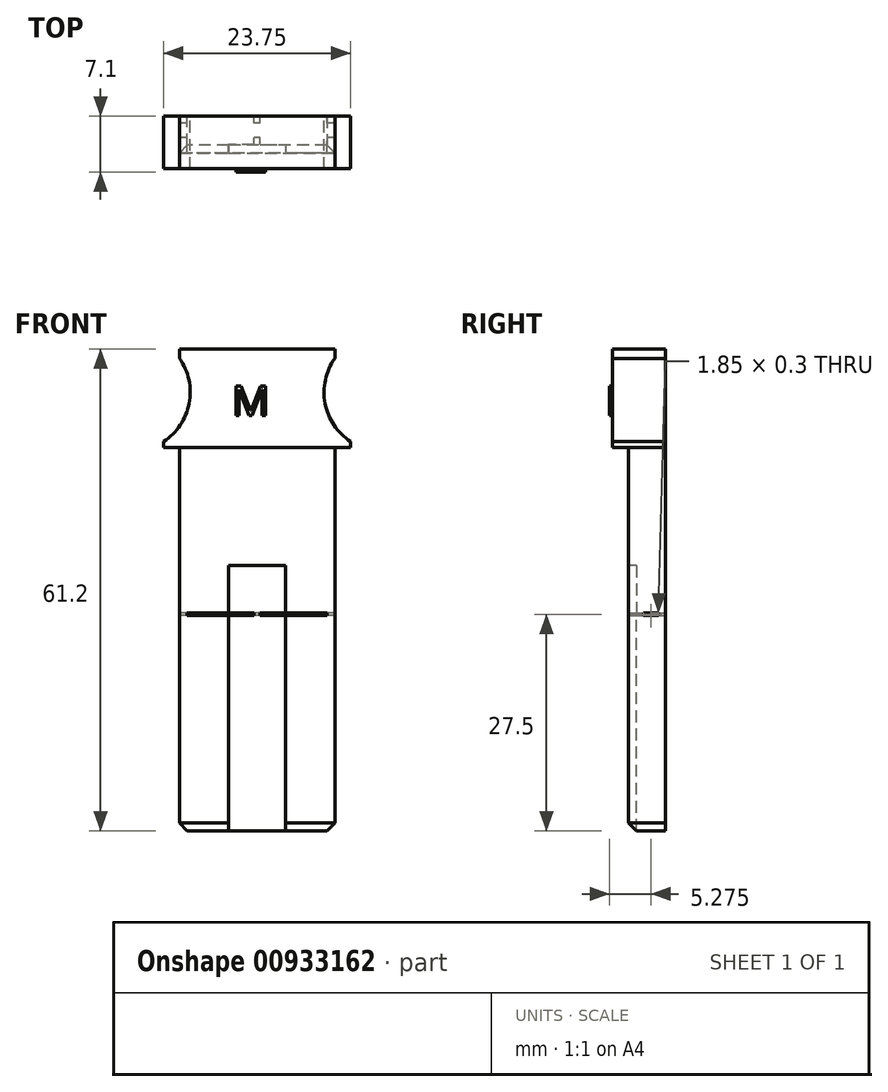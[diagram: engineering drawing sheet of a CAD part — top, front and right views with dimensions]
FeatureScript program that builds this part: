
annotation { "Feature Type Name" : "Feature", "Feature Type Description" : "" }
export const myFeature = defineFeature(function(context is Context, id is Id, definition is map)
    precondition{}
    {
        {
            var Q0;
            Q0=qCreatedBy(makeId("Front.planeOp"),FACE);
            var sketch = newSketch(context, id + "F0", { "sketchPlane" : qUnion([Q0])});
            skLineSegment(sketch, "E0.bottom", {"start": v(0, 0) * mm, "end": v(19.75, 0) * mm});
            skLineSegment(sketch, "E0.top", {"start": v(0, 61.2) * mm, "end": v(19.75, 61.2) * mm});
            skLineSegment(sketch, "E0.left", {"start": v(0, 0) * mm, "end": v(0, 61.2) * mm});
            skLineSegment(sketch, "E0.right", {"start": v(19.75, 0) * mm, "end": v(19.75, 61.2) * mm});
            skLineSegment(sketch, "E1", {"start": v(9.88, 61.2) * mm, "end": v(9.87, 0) * mm, "construction": true});
            skPoint(sketch, "E2", {"position": v(9.88, 34.7) * mm});
            skLineSegment(sketch, "E3", {"start": v(-7.67, 27.5) * mm, "end": v(34.9, 27.5) * mm, "construction": true});
            skLineSegment(sketch, "E4", {"start": v(0, 27.35) * mm, "end": v(0, 27.65) * mm});
            skCircle(sketch, "E5", {"center": v(25.88, 55.7) * mm, "radius": 7.5 * mm});
            skCircle(sketch, "E6.MirrorC", {"center": v(-6.13, 55.7) * mm, "radius": 7.5 * mm});
            skLineSegment(sketch, "E7.bottom", {"start": v(0, 27.65) * mm, "end": v(9.47, 27.65) * mm});
            skLineSegment(sketch, "E7.top", {"start": v(0, 27.65) * mm, "end": v(9.47, 27.65) * mm});
            skLineSegment(sketch, "E7.left", {"start": v(0, 27.65) * mm, "end": v(0, 27.65) * mm});
            skLineSegment(sketch, "E7.right", {"start": v(9.47, 27.65) * mm, "end": v(9.47, 27.65) * mm});
            skLineSegment(sketch, "E8", {"start": v(9.47, 27.65) * mm, "end": v(9.47, 27.35) * mm});
            skLineSegment(sketch, "E9", {"start": v(9.47, 27.35) * mm, "end": v(0, 27.35) * mm});
            skLineSegment(sketch, "E10", {"start": v(0, 27.65) * mm, "end": v(0, 27.35) * mm});
            skLineSegment(sketch, "E11.MirrorCS", {"start": v(19.75, 27.65) * mm, "end": v(10.28, 27.65) * mm});
            skLineSegment(sketch, "E12.MirrorCS", {"start": v(10.27, 27.65) * mm, "end": v(10.27, 27.35) * mm});
            skLineSegment(sketch, "E13.MirrorCS", {"start": v(10.28, 27.35) * mm, "end": v(19.75, 27.35) * mm});
            skLineSegment(sketch, "E14.MirrorCS", {"start": v(19.75, 27.65) * mm, "end": v(19.75, 27.35) * mm});
            skLineSegment(sketch, "E15.bottom", {"start": v(0, 48.7) * mm, "end": v(-2, 48.7) * mm});
            skLineSegment(sketch, "E15.top", {"start": v(0, 65.03) * mm, "end": v(-2, 65.03) * mm});
            skLineSegment(sketch, "E15.left", {"start": v(0, 48.7) * mm, "end": v(0, 65.03) * mm});
            skLineSegment(sketch, "E15.right", {"start": v(-2, 48.7) * mm, "end": v(-2, 65.03) * mm});
            skLineSegment(sketch, "E16.MirrorCS", {"start": v(19.75, 65.03) * mm, "end": v(21.75, 65.03) * mm});
            skLineSegment(sketch, "E17.MirrorCS", {"start": v(21.75, 48.7) * mm, "end": v(21.75, 65.03) * mm});
            skLineSegment(sketch, "E18.MirrorCS", {"start": v(19.75, 48.7) * mm, "end": v(21.75, 48.7) * mm});
            skLineSegment(sketch, "E19", {"start": v(1, 27.65) * mm, "end": v(1, 27.35) * mm});
            skLineSegment(sketch, "E20.MirrorCS", {"start": v(18.75, 27.65) * mm, "end": v(18.75, 27.35) * mm});
            skSolve(sketch);
        }
        {
            var Q0;
            {var subQ4=sQuery(id+"F0.wireOp",EDGE,"E0.bottom");Q0=makeQuery(id+"F0.imprint","IMPRINT",FACE,{"disambiguationData":[TD([[makeQuery(id+"F0.imprint","IMPRINT",EDGE,{"derivedFrom":subQ4}),1.0]])]});}
            var Q1;
            {var subQ0=sQuery(id+"F0.wireOp",EDGE,"E15.bottom");Q1=makeQuery(id+"F0.imprint","IMPRINT",FACE,{"disambiguationData":[TD([[makeQuery(id+"F0.imprint","IMPRINT",EDGE,{"derivedFrom":subQ0}),-1.0]])]});}
            var Q2;
            {var subQ0=sQuery(id+"F0.wireOp",EDGE,"E18.MirrorCS");Q2=makeQuery(id+"F0.imprint","IMPRINT",FACE,{"disambiguationData":[TD([[makeQuery(id+"F0.imprint","IMPRINT",EDGE,{"derivedFrom":subQ0}),1.0]])]});}
            var Q3;
            {var subQ5=sQuery(id+"F0.wireOp",EDGE,"E19");Q3=makeQuery(id+"F0.imprint","IMPRINT",FACE,{"disambiguationData":[TD([[makeQuery(id+"F0.imprint","IMPRINT",EDGE,{"derivedFrom":subQ5}),-1.0]])]});}
            var Q4;
            {var subQ5=sQuery(id+"F0.wireOp",EDGE,"E20.MirrorCS");Q4=makeQuery(id+"F0.imprint","IMPRINT",FACE,{"disambiguationData":[TD([[makeQuery(id+"F0.imprint","IMPRINT",EDGE,{"derivedFrom":subQ5}),1.0]])]});}
            extrude(context, id + "F1", {"entities" : qUnion([Q0, Q1, Q2, Q3, Q4]), "depth" : 4.7 * mm, "offsetDistance" : 25 * mm});
        }
        {
            var Q0;
            Q0=makeQuery(id+"F1.opExtrude","CAP_FACE",FACE,{"disambiguationData":[OSD([sQuery(id+"F0.wireOp",EDGE,"E0.bottom"),sQuery(id+"F0.wireOp",EDGE,"E0.top"),sQuery(id+"F0.wireOp",EDGE,"E0.left"),sQuery(id+"F0.wireOp",EDGE,"E0.right"),sQuery(id+"F0.wireOp",EDGE,"E5"),sQuery(id+"F0.wireOp",EDGE,"E6.MirrorC"),sQuery(id+"F0.wireOp",EDGE,"E7.bottom"),sQuery(id+"F0.wireOp",EDGE,"E8"),sQuery(id+"F0.wireOp",EDGE,"E9"),sQuery(id+"F0.wireOp",EDGE,"E11.MirrorCS"),sQuery(id+"F0.wireOp",EDGE,"E12.MirrorCS"),sQuery(id+"F0.wireOp",EDGE,"E13.MirrorCS"),sQuery(id+"F0.wireOp",EDGE,"E15.bottom"),sQuery(id+"F0.wireOp",EDGE,"E15.right"),sQuery(id+"F0.wireOp",EDGE,"E17.MirrorCS"),sQuery(id+"F0.wireOp",EDGE,"E18.MirrorCS"),sQuery(id+"F0.wireOp",EDGE,"E19"),sQuery(id+"F0.wireOp",EDGE,"E20.MirrorCS")])],"isStart":false});
            var sketch = newSketch(context, id + "F2", { "sketchPlane" : qUnion([Q0])});
            skLineSegment(sketch, "E21", {"start": v(6.28, 33.7) * mm, "end": v(13.48, 33.7) * mm});
            skLineSegment(sketch, "E22", {"start": v(13.48, 33.7) * mm, "end": v(13.48, 2.2) * mm});
            skLineSegment(sketch, "E23", {"start": v(13.48, 2.2) * mm, "end": v(13.48, 2.2) * mm});
            skLineSegment(sketch, "E24", {"start": v(13.48, 2.2) * mm, "end": v(13.48, 0) * mm});
            skLineSegment(sketch, "E25", {"start": v(13.48, 0) * mm, "end": v(6.28, 0) * mm});
            skLineSegment(sketch, "E26", {"start": v(6.28, 0) * mm, "end": v(6.28, 2.2) * mm});
            skLineSegment(sketch, "E27", {"start": v(6.28, 2.2) * mm, "end": v(6.28, 2.2) * mm});
            skLineSegment(sketch, "E28", {"start": v(6.28, 2.2) * mm, "end": v(6.28, 33.7) * mm});
            skLineSegment(sketch, "E29", {"start": v(9.88, 61.2) * mm, "end": v(9.88, 0) * mm, "construction": true});
            skSolve(sketch);
        }
        {
            var Q0;
            Q0=qSketchRegion(id+"F2",true);
            extrude(context, id + "F3", {"entities" : qUnion([Q0]), "operationType" : NewBodyOperationType.REMOVE, "oppositeDirection" : true, "depth" : 1.05 * mm, "offsetDistance" : 25 * mm});
        }
        {
            var Q0;
            {var subQ0=sQuery(id+"F0.wireOp",EDGE,"E0.right");Q0=makeQuery(id+"F1.opExtrude","SWEPT_FACE",FACE,{"disambiguationData":[OSD([subQ0]),TDD([makeQuery(id+"F0.imprint","IMPRINT",EDGE,{"disambiguationData":[TD([[makeQuery(id+"F0.imprint","INTERSECT",VERTEX,{"derivedFrom":[sQuery(id+"F0.wireOp",EDGE,"E0.top"),subQ0]}),1.0]])],"derivedFrom":subQ0})])]});}
            var sketch = newSketch(context, id + "F4", { "sketchPlane" : qUnion([Q0])});
            skLineSegment(sketch, "E30", {"start": v(-15.64, 31.3) * mm, "end": v(17.74, 31.3) * mm, "construction": true});
            skLineSegment(sketch, "E31", {"start": v(-1, 31.3) * mm, "end": v(0, 32.3) * mm});
            skLineSegment(sketch, "E32", {"start": v(0, 32.3) * mm, "end": v(0, 30.3) * mm});
            skLineSegment(sketch, "E33", {"start": v(0, 30.3) * mm, "end": v(-1, 31.3) * mm});
            skSolve(sketch);
        }
        {
            var Q0;
            Q0=makeQuery(id+"F1.opExtrude","CAP_FACE",FACE,{"disambiguationData":[OSD([sQuery(id+"F0.wireOp",EDGE,"E0.bottom"),sQuery(id+"F0.wireOp",EDGE,"E0.top"),sQuery(id+"F0.wireOp",EDGE,"E0.left"),sQuery(id+"F0.wireOp",EDGE,"E0.right"),sQuery(id+"F0.wireOp",EDGE,"E5"),sQuery(id+"F0.wireOp",EDGE,"E6.MirrorC"),sQuery(id+"F0.wireOp",EDGE,"E7.bottom"),sQuery(id+"F0.wireOp",EDGE,"E8"),sQuery(id+"F0.wireOp",EDGE,"E9"),sQuery(id+"F0.wireOp",EDGE,"E11.MirrorCS"),sQuery(id+"F0.wireOp",EDGE,"E12.MirrorCS"),sQuery(id+"F0.wireOp",EDGE,"E13.MirrorCS"),sQuery(id+"F0.wireOp",EDGE,"E15.bottom"),sQuery(id+"F0.wireOp",EDGE,"E15.right"),sQuery(id+"F0.wireOp",EDGE,"E17.MirrorCS"),sQuery(id+"F0.wireOp",EDGE,"E18.MirrorCS"),sQuery(id+"F0.wireOp",EDGE,"E19"),sQuery(id+"F0.wireOp",EDGE,"E20.MirrorCS")])],"isStart":false});
            var sketch = newSketch(context, id + "F5", { "sketchPlane" : qUnion([Q0])});
            skLineSegment(sketch, "E34", {"start": v(0, 48.7) * mm, "end": v(19.75, 48.7) * mm});
            skSolve(sketch);
        }
        {
            var Q0;
            Q0=makeQuery(id+"F5.imprint","IMPRINT",FACE,{"disambiguationData":[TD([[makeQuery(id+"F5.imprint","IMPRINT",EDGE,{"derivedFrom":sQuery(id+"F5.wireOp",EDGE,"E34")}),1.0]])]});
            extrude(context, id + "F6", {"entities" : qUnion([Q0]), "operationType" : NewBodyOperationType.ADD, "depth" : 2 * mm, "offsetDistance" : 25 * mm});
        }
        {
            var Q0;
            Q0=makeQuery(id+"F1.opExtrude","SWEPT_EDGE",EDGE,{"disambiguationData":[OSD([sQuery(id+"F0.wireOp",EDGE,"E0.bottom"),sQuery(id+"F0.wireOp",EDGE,"E0.left")])]});
            var Q1;
            Q1=makeQuery(id+"F1.opExtrude","SWEPT_EDGE",EDGE,{"disambiguationData":[OSD([sQuery(id+"F0.wireOp",EDGE,"E0.bottom"),sQuery(id+"F0.wireOp",EDGE,"E0.right")])]});
            var Q2;
            {var subQ0=sQuery(id+"F0.wireOp",EDGE,"E0.bottom");Q2=makeQuery(id+"F3.boolean.opBoolean","SPLIT",EDGE,{"disambiguationData":[TD([makeQuery(id+"F3.opExtrude","SWEPT_FACE",FACE,{"disambiguationData":[OSD([sQuery(id+"F2.wireOp",EDGE,"E26"),sQuery(id+"F2.wireOp",EDGE,"E28")])]})])],"derivedFrom":makeQuery(id+"F1.opExtrude","CAP_EDGE",EDGE,{"disambiguationData":[OSD([subQ0])],"isStart":false})});}
            var Q3;
            {var subQ0=sQuery(id+"F0.wireOp",EDGE,"E0.bottom");Q3=makeQuery(id+"F3.boolean.opBoolean","SPLIT",EDGE,{"disambiguationData":[TD([makeQuery(id+"F3.opExtrude","SWEPT_FACE",FACE,{"disambiguationData":[OSD([sQuery(id+"F2.wireOp",EDGE,"E22"),sQuery(id+"F2.wireOp",EDGE,"E24")])]})])],"derivedFrom":makeQuery(id+"F1.opExtrude","CAP_EDGE",EDGE,{"disambiguationData":[OSD([subQ0])],"isStart":false})});}
            var Q4;
            Q4=makeQuery(id+"F3.boolean.opBoolean","COPY",EDGE,{"derivedFrom":makeQuery(id+"F3.opExtrude","CAP_EDGE",EDGE,{"disambiguationData":[OSD([sQuery(id+"F2.wireOp",EDGE,"E25")])],"isStart":false})});
            chamfer(context, id + "F7", {"entities" : qUnion([Q0, Q1, Q2, Q3, Q4]), "width" : 1 * mm, "tangentPropagation" : true});
        }
        {
            var Q0;
            Q0=makeQuery(id+"F1.opExtrude","SWEPT_FACE",FACE,{"disambiguationData":[OSD([sQuery(id+"F0.wireOp",EDGE,"E8")])]});
            var sketch = newSketch(context, id + "F8", { "sketchPlane" : qUnion([Q0])});
            skLineSegment(sketch, "E35.bottom", {"start": v(0.9, 27.65) * mm, "end": v(2.75, 27.65) * mm});
            skLineSegment(sketch, "E35.top", {"start": v(0.9, 27.35) * mm, "end": v(2.75, 27.35) * mm});
            skLineSegment(sketch, "E35.left", {"start": v(0.9, 27.65) * mm, "end": v(0.9, 27.35) * mm});
            skLineSegment(sketch, "E35.right", {"start": v(2.75, 27.65) * mm, "end": v(2.75, 27.35) * mm});
            skLineSegment(sketch, "E36", {"start": v(0, 27.65) * mm, "end": v(0.9, 27.65) * mm, "construction": true});
            skLineSegment(sketch, "E37", {"start": v(2.75, 27.65) * mm, "end": v(3.65, 27.65) * mm, "construction": true});
            skSolve(sketch);
        }
        {
            var Q0;
            Q0=qSketchRegion(id+"F8",true);
            extrude(context, id + "F9", {"entities" : qUnion([Q0]), "operationType" : NewBodyOperationType.REMOVE, "endBound" : BoundingType.SYMMETRIC, "oppositeDirection" : true, "depth" : 250 * mm, "offsetDistance" : 25 * mm});
        }
        {
            var Q0;
            Q0=makeQuery(id+"F6.opExtrude","CAP_FACE",FACE,{"disambiguationData":[OSD([sQuery(id+"F0.wireOp",EDGE,"E0.top"),sQuery(id+"F0.wireOp",EDGE,"E0.left"),sQuery(id+"F0.wireOp",EDGE,"E0.right"),sQuery(id+"F0.wireOp",EDGE,"E5"),sQuery(id+"F0.wireOp",EDGE,"E6.MirrorC"),sQuery(id+"F0.wireOp",EDGE,"E15.bottom"),sQuery(id+"F0.wireOp",EDGE,"E15.right"),sQuery(id+"F0.wireOp",EDGE,"E17.MirrorCS"),sQuery(id+"F0.wireOp",EDGE,"E18.MirrorCS"),sQuery(id+"F5.wireOp",EDGE,"E34")])],"isStart":false});
            var sketch = newSketch(context, id + "F10", { "sketchPlane" : qUnion([Q0])});
            skText(sketch, "E38", { "text": "M", "fontName": "OpenSans-Regular.ttf"});
            const initialGuessF10  = {"E38": [0.00667, 0.05273, 1, 0, 0.00382]};
            skSetInitialGuess(sketch, initialGuessF10);
            skSolve(sketch);
        }
        {
            var Q0;
            Q0 = qSketchRegion(id + "F10", true);
            extrude(context, id + "F11", {"entities" : qUnion([Q0]), "operationType" : NewBodyOperationType.ADD, "depth" : 0.4 * mm, "offsetDistance" : 25 * mm});
        }
    });
